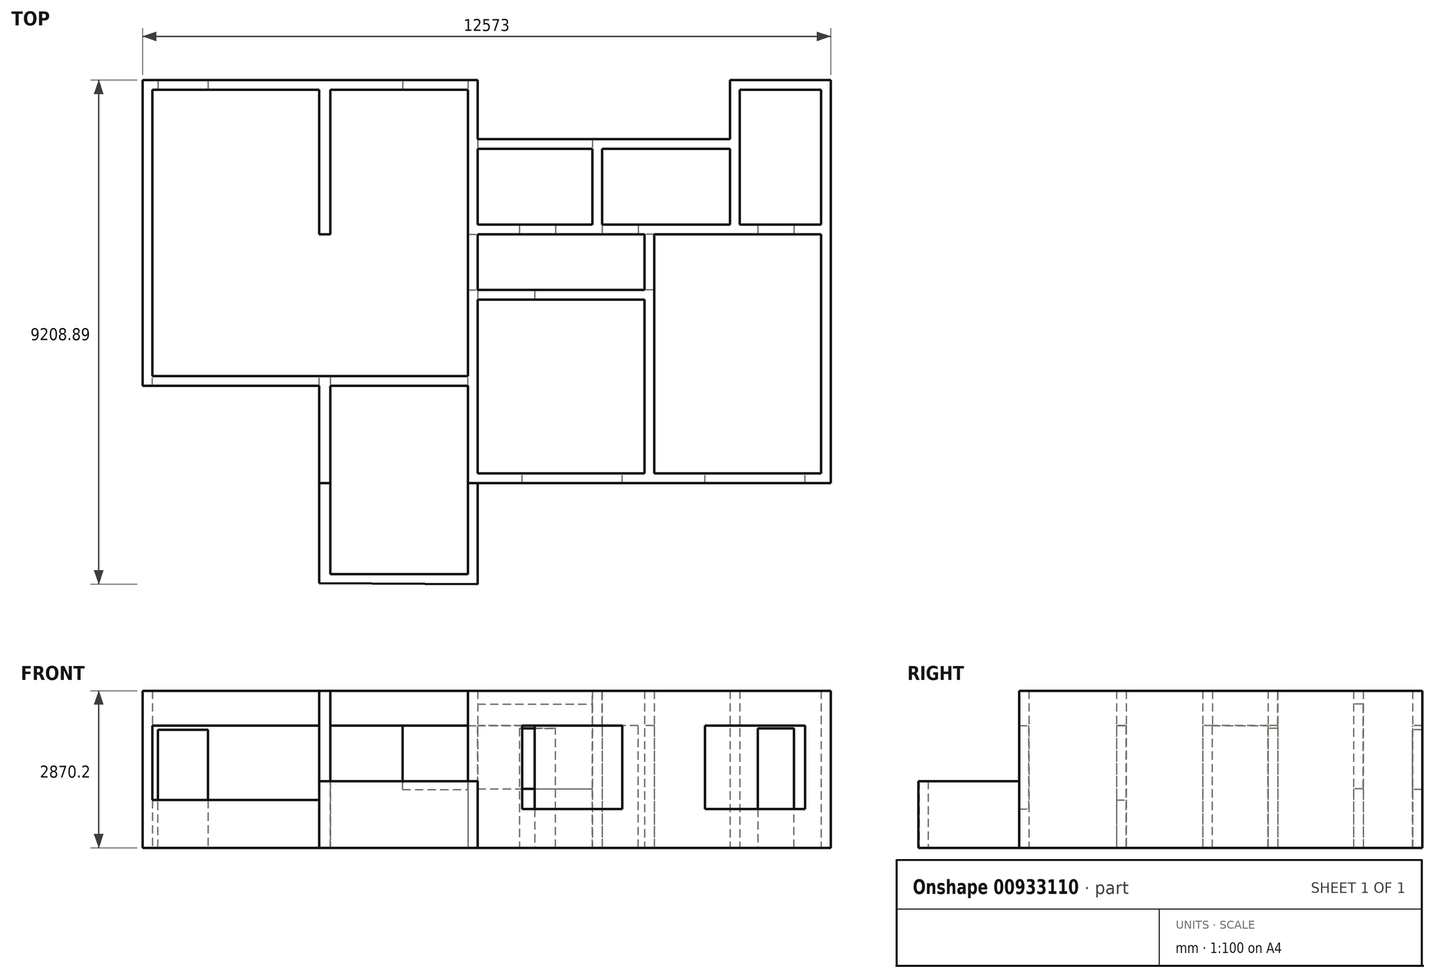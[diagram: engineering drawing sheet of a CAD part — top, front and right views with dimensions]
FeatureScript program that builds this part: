
annotation { "Feature Type Name" : "Feature", "Feature Type Description" : "" }
export const myFeature = defineFeature(function(context is Context, id is Id, definition is map)
    precondition{}
    {
        {
            var Q0;
            Q0=qCreatedBy(makeId("Top.planeOp"),FACE);
            var sketch = newSketch(context, id + "F0", { "sketchPlane" : qUnion([Q0])});
            skLineSegment(sketch, "E0", {"start": v(0, 0) * mm, "end": v(0, 5232.4) * mm});
            skLineSegment(sketch, "E1", {"start": v(0, 5232.4) * mm, "end": v(3048, 5232.4) * mm});
            skLineSegment(sketch, "E2", {"start": v(3048, 5232.4) * mm, "end": v(3048, 2590.8) * mm});
            skLineSegment(sketch, "E3", {"start": v(3251.2, 5232.4) * mm, "end": v(3251.2, 2590.8) * mm});
            skLineSegment(sketch, "E4", {"start": v(3251.2, 2590.8) * mm, "end": v(3048, 2590.8) * mm});
            skLineSegment(sketch, "E5", {"start": v(3251.2, 5232.4) * mm, "end": v(5765.8, 5232.4) * mm});
            skLineSegment(sketch, "E6", {"start": v(5765.8, 0.57) * mm, "end": v(5765.8, 1575.37) * mm});
            skLineSegment(sketch, "E7", {"start": v(5765.8, 5232.4) * mm, "end": v(5765.8, 2590.8) * mm});
            skLineSegment(sketch, "E8", {"start": v(5943.6, 1575.37) * mm, "end": v(8991.6, 1575.37) * mm});
            skLineSegment(sketch, "E9", {"start": v(5943.63, -1777.43) * mm, "end": v(8991.6, -1777.43) * mm});
            skLineSegment(sketch, "E10", {"start": v(9169.4, -1777.43) * mm, "end": v(12217.4, -1777.43) * mm});
            skLineSegment(sketch, "E11", {"start": v(12217.4, -1777.43) * mm, "end": v(12217.4, 2591.37) * mm});
            skLineSegment(sketch, "E12", {"start": v(10553.7, 4153.47) * mm, "end": v(8064.5, 4153.47) * mm});
            skLineSegment(sketch, "E13", {"start": v(10731.5, 5232.97) * mm, "end": v(12217.4, 5232.97) * mm});
            skLineSegment(sketch, "E14", {"start": v(7886.7, 4153.47) * mm, "end": v(5943.6, 4153.47) * mm});
            skLineSegment(sketch, "E15", {"start": v(8991.6, 1575.37) * mm, "end": v(8991.6, 2591.37) * mm});
            skLineSegment(sketch, "E16", {"start": v(5943.6, 2591.37) * mm, "end": v(5943.6, 1575.37) * mm});
            skLineSegment(sketch, "E17", {"start": v(5765.8, 2590.8) * mm, "end": v(5765.8, 1575.37) * mm});
            skLineSegment(sketch, "E18", {"start": v(5943.6, 1397.57) * mm, "end": v(8991.6, 1397.57) * mm});
            skLineSegment(sketch, "E19", {"start": v(8991.6, 1397.57) * mm, "end": v(8991.6, -1777.43) * mm});
            skLineSegment(sketch, "E20", {"start": v(5943.6, 1397.57) * mm, "end": v(5943.63, -1777.43) * mm});
            skLineSegment(sketch, "E21", {"start": v(9169.4, -1777.43) * mm, "end": v(9169.4, 2591.37) * mm});
            skLineSegment(sketch, "E22", {"start": v(5943.6, 4153.47) * mm, "end": v(5943.6, 2769.17) * mm});
            skLineSegment(sketch, "E23", {"start": v(7886.7, 4153.47) * mm, "end": v(7886.7, 2769.17) * mm});
            skLineSegment(sketch, "E24", {"start": v(8064.5, 4153.47) * mm, "end": v(8064.5, 2769.17) * mm});
            skLineSegment(sketch, "E25", {"start": v(5943.6, 2769.17) * mm, "end": v(7886.7, 2769.17) * mm});
            skLineSegment(sketch, "E26", {"start": v(8064.5, 2769.17) * mm, "end": v(10553.7, 2769.17) * mm});
            skLineSegment(sketch, "E27", {"start": v(10553.7, 4153.47) * mm, "end": v(10553.7, 2769.17) * mm});
            skLineSegment(sketch, "E28", {"start": v(5943.6, 2591.37) * mm, "end": v(8991.6, 2591.37) * mm});
            skLineSegment(sketch, "E29", {"start": v(9169.4, 2591.37) * mm, "end": v(12217.4, 2591.37) * mm});
            skLineSegment(sketch, "E30", {"start": v(-177.8, -177.8) * mm, "end": v(-177.8, 5410.2) * mm});
            skLineSegment(sketch, "E31", {"start": v(-177.8, 5410.2) * mm, "end": v(5943.6, 5410.84) * mm});
            skLineSegment(sketch, "E32", {"start": v(10553.7, 4331.34) * mm, "end": v(5943.6, 4331.34) * mm});
            skLineSegment(sketch, "E33", {"start": v(5943.6, 5410.84) * mm, "end": v(5943.6, 4331.34) * mm});
            skLineSegment(sketch, "E34", {"start": v(10553.7, 4331.34) * mm, "end": v(10553.7, 5410.84) * mm});
            skLineSegment(sketch, "E35", {"start": v(10553.7, 5410.84) * mm, "end": v(12395.2, 5410.84) * mm});
            skLineSegment(sketch, "E36", {"start": v(5770.84, -3619.48) * mm, "end": v(3251.23, -3619.5) * mm});
            skLineSegment(sketch, "E37", {"start": v(-177.8, -177.8) * mm, "end": v(3048, -177.8) * mm});
            skLineSegment(sketch, "E38", {"start": v(3048, -177.8) * mm, "end": v(3048.03, -3785.2) * mm});
            skLineSegment(sketch, "E39", {"start": v(12395.2, 5410.84) * mm, "end": v(12395.2, -1955.23) * mm});
            skLineSegment(sketch, "E40", {"start": v(12395.2, -1955.23) * mm, "end": v(5943.6, -1955.23) * mm});
            skLineSegment(sketch, "E41", {"start": v(5943.6, -1955.23) * mm, "end": v(5943.6, -3798.05) * mm});
            skLineSegment(sketch, "E42", {"start": v(3048.03, -3785.2) * mm, "end": v(5943.6, -3798.05) * mm});
            skLineSegment(sketch, "E43", {"start": v(3251.21, -177.8) * mm, "end": v(5765.81, -177.8) * mm});
            skLineSegment(sketch, "E44", {"start": v(3251.21, -177.8) * mm, "end": v(3251.23, -3619.5) * mm});
            skLineSegment(sketch, "E45", {"start": v(0, 0) * mm, "end": v(5765.8, 0.57) * mm});
            skLineSegment(sketch, "E46", {"start": v(5765.81, -177.8) * mm, "end": v(5770.84, -3619.48) * mm});
            skLineSegment(sketch, "E47", {"start": v(10731.5, 5232.97) * mm, "end": v(10731.5, 2769.17) * mm});
            skLineSegment(sketch, "E48", {"start": v(12217.4, 5232.97) * mm, "end": v(12217.4, 2769.17) * mm});
            skLineSegment(sketch, "E49", {"start": v(12217.4, 2769.17) * mm, "end": v(10731.5, 2769.17) * mm});
            skSolve(sketch);
        }
        {
            var Q0;
            Q0=makeQuery(id+"F0.imprint","IMPRINT",FACE,{"disambiguationData":[TD([[makeQuery(id+"F0.imprint","IMPRINT",EDGE,{"derivedFrom":sQuery(id+"F0.wireOp",EDGE,"E0")}),1.0]])]});
            extrude(context, id + "F1", {"entities" : qUnion([Q0]), "depth" : 2870.2 * mm, "offsetDistance" : 25.4 * mm});
        }
        {
            var Q0;
            Q0=makeQuery(id+"F1.opExtrude","SWEPT_FACE",FACE,{"disambiguationData":[OSD([sQuery(id+"F0.wireOp",EDGE,"E1")])]});
            var sketch = newSketch(context, id + "F2", { "sketchPlane" : qUnion([Q0])});
            skLineSegment(sketch, "E50", {"start": v(101.6, 0) * mm, "end": v(101.6, 2159) * mm});
            skLineSegment(sketch, "E51", {"start": v(101.6, 2159) * mm, "end": v(1016, 2159) * mm});
            skLineSegment(sketch, "E52", {"start": v(1016, 2159) * mm, "end": v(1016, 0) * mm});
            skLineSegment(sketch, "E53", {"start": v(1016, 0) * mm, "end": v(101.6, 0) * mm});
            skSolve(sketch);
        }
        {
            var Q0;
            Q0=makeQuery(id+"F2.imprint","IMPRINT",FACE,{"disambiguationData":[TD([[makeQuery(id+"F2.imprint","IMPRINT",EDGE,{"derivedFrom":sQuery(id+"F2.wireOp",EDGE,"E50")}),-1.0]])]});
            extrude(context, id + "F3", {"entities" : qUnion([Q0]), "operationType" : NewBodyOperationType.REMOVE, "endBound" : BoundingType.THROUGH_ALL, "oppositeDirection" : true, "depth" : 25.4 * mm, "offsetDistance" : 25.4 * mm});
        }
        {
            var Q0;
            Q0=makeQuery(id+"F1.opExtrude","SWEPT_FACE",FACE,{"disambiguationData":[OSD([sQuery(id+"F0.wireOp",EDGE,"E45")])]});
            var sketch = newSketch(context, id + "F4", { "sketchPlane" : qUnion([Q0])});
            skLineSegment(sketch, "E54", {"start": v(0, 2870.2) * mm, "end": v(0, 2235.2) * mm});
            skLineSegment(sketch, "E55", {"start": v(0, 2235.2) * mm, "end": v(0, 872.46) * mm});
            skLineSegment(sketch, "E56", {"start": v(0, 2235.2) * mm, "end": v(-2456.97, 2235.2) * mm});
            skLineSegment(sketch, "E57", {"start": v(-2456.97, 2235.2) * mm, "end": v(-2456.97, 872.46) * mm});
            skLineSegment(sketch, "E58", {"start": v(-2456.97, 872.46) * mm, "end": v(0, 872.46) * mm});
            skSolve(sketch);
        }
        {
            var Q0;
            Q0=makeQuery(id+"F4.imprint","IMPRINT",FACE,{"disambiguationData":[TD([[makeQuery(id+"F4.imprint","IMPRINT",EDGE,{"derivedFrom":sQuery(id+"F4.wireOp",EDGE,"E55")}),-1.0]])]});
            extrude(context, id + "F5", {"entities" : qUnion([Q0]), "operationType" : NewBodyOperationType.REMOVE, "endBound" : BoundingType.THROUGH_ALL, "oppositeDirection" : true, "depth" : 25.4 * mm, "offsetDistance" : 25.4 * mm});
        }
        {
            var Q0;
            Q0=makeQuery(id+"F5.boolean.opBoolean","COPY",FACE,{"derivedFrom":makeQuery(id+"F5.opExtrude","SWEPT_FACE",FACE,{"disambiguationData":[OSD([sQuery(id+"F4.wireOp",EDGE,"E57")])]})});
            var Q1;
            Q1=makeQuery(id+"F1.opExtrude","SWEPT_FACE",FACE,{"disambiguationData":[OSD([sQuery(id+"F0.wireOp",EDGE,"E38")])]});
            extrude(context, id + "F6", {"entities" : qUnion([Q0]), "operationType" : NewBodyOperationType.REMOVE, "endBound" : BoundingType.UP_TO_SURFACE, "oppositeDirection" : true, "depth" : 25.4 * mm, "endBoundEntityFace" : qUnion([Q1]), "offsetDistance" : 25.4 * mm});
        }
        {
            var Q0;
            Q0=makeQuery(id+"F1.opExtrude","SWEPT_FACE",FACE,{"disambiguationData":[OSD([sQuery(id+"F0.wireOp",EDGE,"E45")])]});
            var sketch = newSketch(context, id + "F7", { "sketchPlane" : qUnion([Q0])});
            skLineSegment(sketch, "E59", {"start": v(-5765.8, 2235.2) * mm, "end": v(-5765.8, 0) * mm});
            skLineSegment(sketch, "E60", {"start": v(-5765.8, 2235.2) * mm, "end": v(-4114.3, 2235.2) * mm});
            skLineSegment(sketch, "E61", {"start": v(-4114.3, 2235.2) * mm, "end": v(-4114.3, 0) * mm});
            skLineSegment(sketch, "E62", {"start": v(-4114.3, 0) * mm, "end": v(-5765.8, 0) * mm});
            skSolve(sketch);
        }
        {
            var Q0;
            Q0=makeQuery(id+"F7.imprint","IMPRINT",FACE,{"disambiguationData":[TD([[makeQuery(id+"F7.imprint","IMPRINT",EDGE,{"derivedFrom":sQuery(id+"F7.wireOp",EDGE,"E59")}),1.0]])]});
            extrude(context, id + "F8", {"entities" : qUnion([Q0]), "operationType" : NewBodyOperationType.REMOVE, "oppositeDirection" : true, "depth" : 203.2 * mm, "offsetDistance" : 25.4 * mm});
        }
        {
            var Q0;
            Q0=makeQuery(id+"F8.boolean.opBoolean","COPY",FACE,{"derivedFrom":makeQuery(id+"F8.opExtrude","SWEPT_FACE",FACE,{"disambiguationData":[OSD([sQuery(id+"F7.wireOp",EDGE,"E61")])]})});
            var Q1;
            Q1=makeQuery(id+"F1.opExtrude","SWEPT_FACE",FACE,{"disambiguationData":[OSD([sQuery(id+"F0.wireOp",EDGE,"E44")])]});
            extrude(context, id + "F9", {"entities" : qUnion([Q0]), "operationType" : NewBodyOperationType.REMOVE, "endBound" : BoundingType.UP_TO_SURFACE, "oppositeDirection" : true, "depth" : 25.4 * mm, "endBoundEntityFace" : qUnion([Q1]), "offsetDistance" : 25.4 * mm});
        }
        {
            var Q0;
            Q0=makeQuery(id+"F1.opExtrude","SWEPT_FACE",FACE,{"disambiguationData":[OSD([sQuery(id+"F0.wireOp",EDGE,"E42")])]});
            var sketch = newSketch(context, id + "F10", { "sketchPlane" : qUnion([Q0])});
            skLineSegment(sketch, "E63", {"start": v(5960.4, 2870.2) * mm, "end": v(5960.4, 1219.2) * mm});
            skLineSegment(sketch, "E64", {"start": v(2907.05, 2870.2) * mm, "end": v(5960.4, 2870.2) * mm});
            skLineSegment(sketch, "E65", {"start": v(5960.4, 1219.2) * mm, "end": v(5397.9, 1219.2) * mm});
            skLineSegment(sketch, "E66", {"start": v(5397.9, 1219.2) * mm, "end": v(5397.9, 2870.2) * mm});
            skLineSegment(sketch, "E67", {"start": v(5397.9, 2870.2) * mm, "end": v(5960.4, 2870.2) * mm});
            skSolve(sketch);
        }
        {
            var Q0;
            Q0=makeQuery(id+"F1.opExtrude","SWEPT_FACE",FACE,{"disambiguationData":[OSD([sQuery(id+"F0.wireOp",EDGE,"E16")])]});
            var sketch = newSketch(context, id + "F11", { "sketchPlane" : qUnion([Q0])});
            skLineSegment(sketch, "E68", {"start": v(1575.37, 2235.2) * mm, "end": v(1575.37, 0) * mm});
            skLineSegment(sketch, "E69", {"start": v(1575.37, 0) * mm, "end": v(2591.37, 0) * mm});
            skLineSegment(sketch, "E70", {"start": v(2591.37, 0) * mm, "end": v(2591.37, 2235.2) * mm});
            skLineSegment(sketch, "E71", {"start": v(2591.37, 2235.2) * mm, "end": v(1575.37, 2235.2) * mm});
            skSolve(sketch);
        }
        {
            var Q0;
            Q0=makeQuery(id+"F11.imprint","IMPRINT",FACE,{"disambiguationData":[TD([[makeQuery(id+"F11.imprint","IMPRINT",EDGE,{"derivedFrom":sQuery(id+"F11.wireOp",EDGE,"E68")}),1.0]])]});
            extrude(context, id + "F12", {"entities" : qUnion([Q0]), "operationType" : NewBodyOperationType.REMOVE, "oppositeDirection" : true, "depth" : 406.4 * mm, "offsetDistance" : 25.4 * mm});
        }
        {
            var Q0;
            Q0=makeQuery(id+"F1.opExtrude","SWEPT_FACE",FACE,{"disambiguationData":[OSD([sQuery(id+"F0.wireOp",EDGE,"E15")])]});
            var sketch = newSketch(context, id + "F13", { "sketchPlane" : qUnion([Q0])});
            skLineSegment(sketch, "E72", {"start": v(-2591.37, 2870.2) * mm, "end": v(-2591.37, 2235.2) * mm});
            skLineSegment(sketch, "E73", {"start": v(-2591.37, 2235.2) * mm, "end": v(-2591.37, 0) * mm});
            skLineSegment(sketch, "E74", {"start": v(-2591.37, 0) * mm, "end": v(-1575.37, 0) * mm});
            skLineSegment(sketch, "E75", {"start": v(-1575.37, 0) * mm, "end": v(-1575.37, 2235.2) * mm});
            skLineSegment(sketch, "E76", {"start": v(-1575.37, 2235.2) * mm, "end": v(-2591.37, 2235.2) * mm});
            skSolve(sketch);
        }
        {
            var Q0;
            Q0=makeQuery(id+"F13.imprint","IMPRINT",FACE,{"disambiguationData":[TD([[makeQuery(id+"F13.imprint","IMPRINT",EDGE,{"derivedFrom":sQuery(id+"F13.wireOp",EDGE,"E73")}),1.0]])]});
            extrude(context, id + "F14", {"entities" : qUnion([Q0]), "operationType" : NewBodyOperationType.REMOVE, "oppositeDirection" : true, "depth" : 457.2 * mm, "offsetDistance" : 25.4 * mm});
        }
        {
            var Q0;
            Q0=makeQuery(id+"F1.opExtrude","SWEPT_FACE",FACE,{"disambiguationData":[OSD([sQuery(id+"F0.wireOp",EDGE,"E5")])]});
            var sketch = newSketch(context, id + "F15", { "sketchPlane" : qUnion([Q0])});
            skLineSegment(sketch, "E77", {"start": v(5765.8, 2235.2) * mm, "end": v(5765.8, 1066.8) * mm});
            skLineSegment(sketch, "E78", {"start": v(5765.8, 1066.8) * mm, "end": v(4572, 1066.8) * mm});
            skLineSegment(sketch, "E79", {"start": v(4572, 1066.8) * mm, "end": v(4572, 2235.2) * mm});
            skLineSegment(sketch, "E80", {"start": v(4572, 2235.2) * mm, "end": v(5765.8, 2235.2) * mm});
            skSolve(sketch);
        }
        {
            var Q0;
            Q0=makeQuery(id+"F15.imprint","IMPRINT",FACE,{"disambiguationData":[TD([[makeQuery(id+"F15.imprint","IMPRINT",EDGE,{"derivedFrom":sQuery(id+"F15.wireOp",EDGE,"E77")}),-1.0]])]});
            extrude(context, id + "F16", {"entities" : qUnion([Q0]), "operationType" : NewBodyOperationType.REMOVE, "oppositeDirection" : true, "depth" : 381 * mm, "offsetDistance" : 25.4 * mm});
        }
        {
            var Q0;
            Q0=makeQuery(id+"F14.boolean.opBoolean","MERGE",FACE,{"derivedFrom":[makeQuery(id+"F1.opExtrude","SWEPT_FACE",FACE,{"disambiguationData":[OSD([sQuery(id+"F0.wireOp",EDGE,"E29")])]}),makeQuery(id+"F12.boolean.opBoolean","MERGE",FACE,{"derivedFrom":[makeQuery(id+"F1.opExtrude","SWEPT_FACE",FACE,{"disambiguationData":[OSD([sQuery(id+"F0.wireOp",EDGE,"E28")])]})],"fromTools":[makeQuery(id+"F12.opExtrude","SWEPT_FACE",FACE,{"disambiguationData":[OSD([sQuery(id+"F11.wireOp",EDGE,"E70")])]})]})],"fromTools":[makeQuery(id+"F14.opExtrude","SWEPT_FACE",FACE,{"disambiguationData":[OSD([sQuery(id+"F13.wireOp",EDGE,"E73")])]})]});
            var sketch = newSketch(context, id + "F17", { "sketchPlane" : qUnion([Q0])});
            skLineSegment(sketch, "E81", {"start": v(6707.64, 0) * mm, "end": v(7368.04, 0) * mm});
            skLineSegment(sketch, "E82", {"start": v(7368.04, 0) * mm, "end": v(7368.04, 2184.4) * mm});
            skLineSegment(sketch, "E83", {"start": v(7368.04, 2184.4) * mm, "end": v(6707.64, 2184.4) * mm});
            skLineSegment(sketch, "E84", {"start": v(6707.64, 2184.4) * mm, "end": v(6707.64, 0) * mm});
            skSolve(sketch);
        }
        {
            var Q0;
            Q0=makeQuery(id+"F17.imprint","IMPRINT",FACE,{"disambiguationData":[TD([[makeQuery(id+"F17.imprint","IMPRINT",EDGE,{"derivedFrom":sQuery(id+"F17.wireOp",EDGE,"E81")}),1.0]])]});
            extrude(context, id + "F18", {"entities" : qUnion([Q0]), "operationType" : NewBodyOperationType.REMOVE, "oppositeDirection" : true, "depth" : 330.2 * mm, "offsetDistance" : 25.4 * mm});
        }
        {
            var Q0;
            Q0=makeQuery(id+"F14.boolean.opBoolean","MERGE",FACE,{"derivedFrom":[makeQuery(id+"F1.opExtrude","SWEPT_FACE",FACE,{"disambiguationData":[OSD([sQuery(id+"F0.wireOp",EDGE,"E29")])]}),makeQuery(id+"F12.boolean.opBoolean","MERGE",FACE,{"derivedFrom":[makeQuery(id+"F1.opExtrude","SWEPT_FACE",FACE,{"disambiguationData":[OSD([sQuery(id+"F0.wireOp",EDGE,"E28")])]})],"fromTools":[makeQuery(id+"F12.opExtrude","SWEPT_FACE",FACE,{"disambiguationData":[OSD([sQuery(id+"F11.wireOp",EDGE,"E70")])]})]})],"fromTools":[makeQuery(id+"F14.opExtrude","SWEPT_FACE",FACE,{"disambiguationData":[OSD([sQuery(id+"F13.wireOp",EDGE,"E73")])]})]});
            var sketch = newSketch(context, id + "F19", { "sketchPlane" : qUnion([Q0])});
            skLineSegment(sketch, "E85", {"start": v(8218.94, 0) * mm, "end": v(8879.34, 0) * mm});
            skLineSegment(sketch, "E86", {"start": v(8879.34, 0) * mm, "end": v(8879.34, 2235.2) * mm});
            skLineSegment(sketch, "E87", {"start": v(8879.34, 2235.2) * mm, "end": v(8218.94, 2235.2) * mm});
            skLineSegment(sketch, "E88", {"start": v(8218.94, 2235.2) * mm, "end": v(8218.94, 0) * mm});
            skSolve(sketch);
        }
        {
            var Q0;
            Q0=makeQuery(id+"F19.imprint","IMPRINT",FACE,{"disambiguationData":[TD([[makeQuery(id+"F19.imprint","IMPRINT",EDGE,{"derivedFrom":sQuery(id+"F19.wireOp",EDGE,"E85")}),1.0]])]});
            var Q1;
            Q1=makeQuery(id+"F1.opExtrude","SWEPT_FACE",FACE,{"disambiguationData":[OSD([sQuery(id+"F0.wireOp",EDGE,"E12")])]});
            extrude(context, id + "F20", {"entities" : qUnion([Q0]), "operationType" : NewBodyOperationType.REMOVE, "endBound" : BoundingType.UP_TO_SURFACE, "oppositeDirection" : true, "depth" : 304.8 * mm, "endBoundEntityFace" : qUnion([Q1]), "offsetDistance" : 25.4 * mm});
        }
        {
            var Q0;
            Q0=makeQuery(id+"F1.opExtrude","SWEPT_FACE",FACE,{"disambiguationData":[OSD([sQuery(id+"F0.wireOp",EDGE,"E24")])]});
            extrude(context, id + "F21", {"entities" : qUnion([Q0]), "operationType" : NewBodyOperationType.REMOVE, "oppositeDirection" : true, "depth" : 685.8 * mm, "offsetDistance" : 25.4 * mm});
        }
        {
            var Q0;
            {var subQ0=sQuery(id+"F0.wireOp",EDGE,"E26");Q0=makeQuery(id+"F21.boolean.opBoolean","MERGE",FACE,{"derivedFrom":[makeQuery(id+"F1.opExtrude","SWEPT_FACE",FACE,{"disambiguationData":[OSD([subQ0])]}),makeQuery(id+"F1.opExtrude","SWEPT_FACE",FACE,{"disambiguationData":[OSD([sQuery(id+"F0.wireOp",EDGE,"E25")])]})],"fromTools":[makeQuery(id+"F21.opExtrude","SWEPT_FACE",FACE,{"disambiguationData":[OSD([sQuery(id+"F0.wireOp",EDGE,"E24"),subQ0])]})]});}
            var sketch = newSketch(context, id + "F22", { "sketchPlane" : qUnion([Q0])});
            skLineSegment(sketch, "E89", {"start": v(-8218.94, 0) * mm, "end": v(-8218.94, 2870.2) * mm});
            skLineSegment(sketch, "E90", {"start": v(-8218.94, 2870.2) * mm, "end": v(-8041.14, 2870.2) * mm});
            skLineSegment(sketch, "E91", {"start": v(-8041.14, 2870.2) * mm, "end": v(-8041.14, 0) * mm});
            skLineSegment(sketch, "E92", {"start": v(-8041.14, 0) * mm, "end": v(-8218.94, 0) * mm});
            skSolve(sketch);
        }
        {
            var Q0;
            {var subQ0=sQuery(id+"F22.wireOp",EDGE,"E90");Q0=makeQuery(id+"F22.imprint","IMPRINT",FACE,{"disambiguationData":[TD([[makeQuery(id+"F22.imprint","IMPRINT",EDGE,{"derivedFrom":subQ0}),1.0]])]});}
            var Q1;
            {var subQ0=sQuery(id+"F0.wireOp",EDGE,"E12");Q1=makeQuery(id+"F21.boolean.opBoolean","MERGE",FACE,{"derivedFrom":[makeQuery(id+"F20.boolean.opBoolean","MERGE",FACE,{"derivedFrom":[makeQuery(id+"F1.opExtrude","SWEPT_FACE",FACE,{"disambiguationData":[OSD([subQ0])]}),makeQuery(id+"F1.opExtrude","SWEPT_FACE",FACE,{"disambiguationData":[OSD([sQuery(id+"F0.wireOp",EDGE,"E14")])]})],"fromTools":[makeQuery(id+"F20.opExtrude","CAP_FACE",FACE,{"disambiguationData":[OSD([sQuery(id+"F19.wireOp",EDGE,"E85"),sQuery(id+"F19.wireOp",EDGE,"E86"),sQuery(id+"F19.wireOp",EDGE,"E87"),sQuery(id+"F19.wireOp",EDGE,"E88")])],"isStart":false})]})],"fromTools":[makeQuery(id+"F21.opExtrude","SWEPT_FACE",FACE,{"disambiguationData":[OSD([subQ0,sQuery(id+"F0.wireOp",EDGE,"E24")])]})]});}
            extrude(context, id + "F23", {"entities" : qUnion([Q0]), "operationType" : NewBodyOperationType.ADD, "endBound" : BoundingType.UP_TO_SURFACE, "depth" : 25.4 * mm, "endBoundEntityFace" : qUnion([Q1]), "offsetDistance" : 25.4 * mm});
        }
        {
            var Q0;
            Q0=makeQuery(id+"F14.boolean.opBoolean","MERGE",FACE,{"derivedFrom":[makeQuery(id+"F1.opExtrude","SWEPT_FACE",FACE,{"disambiguationData":[OSD([sQuery(id+"F0.wireOp",EDGE,"E29")])]}),makeQuery(id+"F12.boolean.opBoolean","MERGE",FACE,{"derivedFrom":[makeQuery(id+"F1.opExtrude","SWEPT_FACE",FACE,{"disambiguationData":[OSD([sQuery(id+"F0.wireOp",EDGE,"E28")])]})],"fromTools":[makeQuery(id+"F12.opExtrude","SWEPT_FACE",FACE,{"disambiguationData":[OSD([sQuery(id+"F11.wireOp",EDGE,"E70")])]})]})],"fromTools":[makeQuery(id+"F14.opExtrude","SWEPT_FACE",FACE,{"disambiguationData":[OSD([sQuery(id+"F13.wireOp",EDGE,"E73")])]})]});
            var sketch = newSketch(context, id + "F24", { "sketchPlane" : qUnion([Q0])});
            skLineSegment(sketch, "E93", {"start": v(11723.04, 0) * mm, "end": v(11723.04, 2184.4) * mm});
            skLineSegment(sketch, "E94", {"start": v(11723.04, 2184.4) * mm, "end": v(11062.64, 2184.4) * mm});
            skLineSegment(sketch, "E95", {"start": v(11062.64, 2184.4) * mm, "end": v(11062.64, 0) * mm});
            skLineSegment(sketch, "E96", {"start": v(11062.64, 0) * mm, "end": v(11723.04, 0) * mm});
            skSolve(sketch);
        }
        {
            var Q0;
            Q0=makeQuery(id+"F24.imprint","IMPRINT",FACE,{"disambiguationData":[TD([[makeQuery(id+"F24.imprint","IMPRINT",EDGE,{"derivedFrom":sQuery(id+"F24.wireOp",EDGE,"E93")}),1.0]])]});
            extrude(context, id + "F25", {"entities" : qUnion([Q0]), "operationType" : NewBodyOperationType.REMOVE, "oppositeDirection" : true, "depth" : 381 * mm, "offsetDistance" : 25.4 * mm});
        }
        {
            var Q0;
            Q0=makeQuery(id+"F1.opExtrude","SWEPT_FACE",FACE,{"disambiguationData":[OSD([sQuery(id+"F0.wireOp",EDGE,"E18")])]});
            var sketch = newSketch(context, id + "F26", { "sketchPlane" : qUnion([Q0])});
            skLineSegment(sketch, "E97", {"start": v(5943.6, 2235.2) * mm, "end": v(6984.7, 2235.2) * mm});
            skLineSegment(sketch, "E98", {"start": v(6984.7, 2235.2) * mm, "end": v(6984.7, 0) * mm});
            skLineSegment(sketch, "E99", {"start": v(6984.7, 0) * mm, "end": v(5943.6, 0) * mm});
            skLineSegment(sketch, "E100", {"start": v(5943.6, 0) * mm, "end": v(5943.6, 2235.2) * mm});
            skSolve(sketch);
        }
        {
            var Q0;
            Q0=makeQuery(id+"F26.imprint","IMPRINT",FACE,{"disambiguationData":[TD([[makeQuery(id+"F26.imprint","IMPRINT",EDGE,{"derivedFrom":sQuery(id+"F26.wireOp",EDGE,"E97")}),-1.0]])]});
            extrude(context, id + "F27", {"entities" : qUnion([Q0]), "operationType" : NewBodyOperationType.REMOVE, "oppositeDirection" : true, "depth" : 279.4 * mm, "offsetDistance" : 25.4 * mm});
        }
        {
            var Q0;
            Q0=makeQuery(id+"F1.opExtrude","SWEPT_FACE",FACE,{"disambiguationData":[OSD([sQuery(id+"F0.wireOp",EDGE,"E9")])]});
            var sketch = newSketch(context, id + "F28", { "sketchPlane" : qUnion([Q0])});
            skLineSegment(sketch, "E101", {"start": v(-8586.37, 2235.2) * mm, "end": v(-6757.57, 2235.2) * mm});
            skLineSegment(sketch, "E102", {"start": v(-6757.57, 2235.2) * mm, "end": v(-6757.57, 711.2) * mm});
            skLineSegment(sketch, "E103", {"start": v(-6757.57, 711.2) * mm, "end": v(-8586.37, 711.2) * mm});
            skLineSegment(sketch, "E104", {"start": v(-8586.37, 711.2) * mm, "end": v(-8586.37, 2235.2) * mm});
            skSolve(sketch);
        }
        {
            var Q0;
            Q0=makeQuery(id+"F28.imprint","IMPRINT",FACE,{"disambiguationData":[TD([[makeQuery(id+"F28.imprint","IMPRINT",EDGE,{"derivedFrom":sQuery(id+"F28.wireOp",EDGE,"E101")}),-1.0]])]});
            extrude(context, id + "F29", {"entities" : qUnion([Q0]), "operationType" : NewBodyOperationType.REMOVE, "oppositeDirection" : true, "depth" : 990.6 * mm, "offsetDistance" : 25.4 * mm});
        }
        {
            var Q0;
            Q0=makeQuery(id+"F1.opExtrude","SWEPT_FACE",FACE,{"disambiguationData":[OSD([sQuery(id+"F0.wireOp",EDGE,"E10")])]});
            var sketch = newSketch(context, id + "F30", { "sketchPlane" : qUnion([Q0])});
            skLineSegment(sketch, "E105", {"start": v(-11926.24, 2235.2) * mm, "end": v(-10097.44, 2235.2) * mm});
            skLineSegment(sketch, "E106", {"start": v(-10097.44, 2235.2) * mm, "end": v(-10097.44, 711.2) * mm});
            skLineSegment(sketch, "E107", {"start": v(-10097.44, 711.2) * mm, "end": v(-11926.24, 711.2) * mm});
            skLineSegment(sketch, "E108", {"start": v(-11926.24, 711.2) * mm, "end": v(-11926.24, 2235.2) * mm});
            skSolve(sketch);
        }
        {
            var Q0;
            Q0=makeQuery(id+"F30.imprint","IMPRINT",FACE,{"disambiguationData":[TD([[makeQuery(id+"F30.imprint","IMPRINT",EDGE,{"derivedFrom":sQuery(id+"F30.wireOp",EDGE,"E105")}),-1.0]])]});
            extrude(context, id + "F31", {"entities" : qUnion([Q0]), "operationType" : NewBodyOperationType.REMOVE, "oppositeDirection" : true, "depth" : 304.8 * mm, "offsetDistance" : 25.4 * mm});
        }
        {
            var Q0;
            {var subQ0=sQuery(id+"F0.wireOp",EDGE,"E22");var subQ26=sQuery(id+"F0.wireOp",EDGE,"E24");var subQ35=sQuery(id+"F0.wireOp",EDGE,"E14");var subQ37=sQuery(id+"F0.wireOp",EDGE,"E12");Q0=makeQuery(id+"F23.boolean.opBoolean","SPLIT",FACE,{"disambiguationData":[TD([makeQuery(id+"F1.opExtrude","SWEPT_FACE",FACE,{"disambiguationData":[OSD([subQ0])]})])],"derivedFrom":makeQuery(id+"F21.boolean.opBoolean","MERGE",FACE,{"derivedFrom":[makeQuery(id+"F20.boolean.opBoolean","MERGE",FACE,{"derivedFrom":[makeQuery(id+"F1.opExtrude","SWEPT_FACE",FACE,{"disambiguationData":[OSD([subQ37])]}),makeQuery(id+"F1.opExtrude","SWEPT_FACE",FACE,{"disambiguationData":[OSD([subQ35])]})],"fromTools":[makeQuery(id+"F20.opExtrude","CAP_FACE",FACE,{"disambiguationData":[OSD([sQuery(id+"F19.wireOp",EDGE,"E85"),sQuery(id+"F19.wireOp",EDGE,"E86"),sQuery(id+"F19.wireOp",EDGE,"E87"),sQuery(id+"F19.wireOp",EDGE,"E88")])],"isStart":false})]})],"fromTools":[makeQuery(id+"F21.opExtrude","SWEPT_FACE",FACE,{"disambiguationData":[OSD([subQ37,subQ26])]})]})});}
            var sketch = newSketch(context, id + "F32", { "sketchPlane" : qUnion([Q0])});
            skLineSegment(sketch, "E109", {"start": v(5943.6, 2628.9) * mm, "end": v(8041.14, 2628.9) * mm});
            skLineSegment(sketch, "E110", {"start": v(5943.6, 1079.5) * mm, "end": v(8041.14, 1079.5) * mm});
            skLineSegment(sketch, "E111", {"start": v(5943.6, 2628.9) * mm, "end": v(5943.6, 1079.5) * mm});
            skLineSegment(sketch, "E112", {"start": v(8041.14, 2628.9) * mm, "end": v(8041.14, 1079.5) * mm});
            skSolve(sketch);
        }
        {
            var Q0;
            Q0=makeQuery(id+"F32.imprint","IMPRINT",FACE,{"disambiguationData":[TD([[makeQuery(id+"F32.imprint","IMPRINT",EDGE,{"derivedFrom":sQuery(id+"F32.wireOp",EDGE,"E109")}),-1.0]])]});
            extrude(context, id + "F33", {"entities" : qUnion([Q0]), "operationType" : NewBodyOperationType.REMOVE, "oppositeDirection" : true, "depth" : 304.8 * mm, "offsetDistance" : 25.4 * mm});
        }
        {
            var Q0;
            Q0=makeQuery(id+"F10.imprint","IMPRINT",FACE,{"disambiguationData":[TD([[makeQuery(id+"F10.imprint","IMPRINT",EDGE,{"derivedFrom":sQuery(id+"F10.wireOp",EDGE,"E63")}),-1.0]])]});
            var Q1;
            Q1=makeQuery(id+"F1.opExtrude","SWEPT_FACE",FACE,{"disambiguationData":[OSD([sQuery(id+"F0.wireOp",EDGE,"E40")])]});
            extrude(context, id + "F34", {"entities" : qUnion([Q0]), "operationType" : NewBodyOperationType.REMOVE, "endBound" : BoundingType.UP_TO_SURFACE, "oppositeDirection" : true, "depth" : 25.4 * mm, "endBoundEntityFace" : qUnion([Q1]), "offsetDistance" : 25.4 * mm});
        }
        {
            var Q0;
            Q0=makeQuery(id+"F34.boolean.opBoolean","COPY",FACE,{"derivedFrom":makeQuery(id+"F34.opExtrude","SWEPT_FACE",FACE,{"disambiguationData":[OSD([sQuery(id+"F10.wireOp",EDGE,"E66")])]})});
            var Q1;
            Q1=makeQuery(id+"F1.opExtrude","SWEPT_FACE",FACE,{"disambiguationData":[OSD([sQuery(id+"F0.wireOp",EDGE,"E38")])]});
            extrude(context, id + "F35", {"entities" : qUnion([Q0]), "operationType" : NewBodyOperationType.REMOVE, "endBound" : BoundingType.UP_TO_SURFACE, "oppositeDirection" : true, "depth" : 25.4 * mm, "endBoundEntityFace" : qUnion([Q1]), "offsetDistance" : 25.4 * mm});
        }
        {
            var Q0;
            Q0=makeQuery(id+"F1.opExtrude","SWEPT_FACE",FACE,{"disambiguationData":[OSD([sQuery(id+"F0.wireOp",EDGE,"E38")])]});
            extrude(context, id + "F36", {"entities" : qUnion([Q0]), "operationType" : NewBodyOperationType.ADD, "oppositeDirection" : true, "depth" : 203.2 * mm, "offsetDistance" : 25.4 * mm});
        }
        {
            var Q0;
            Q0=makeQuery(id+"F35.boolean.opBoolean","COPY",FACE,{"derivedFrom":makeQuery(id+"F35.opExtrude","SWEPT_FACE",FACE,{"disambiguationData":[OSD([sQuery(id+"F0.wireOp",EDGE,"E36"),sQuery(id+"F10.wireOp",EDGE,"E66")])]})});
            var Q1;
            Q1=makeQuery(id+"F34.boolean.opBoolean","MERGE",FACE,{"derivedFrom":[makeQuery(id+"F1.opExtrude","SWEPT_FACE",FACE,{"disambiguationData":[OSD([sQuery(id+"F0.wireOp",EDGE,"E40")])]})],"fromTools":[makeQuery(id+"F34.opExtrude","CAP_FACE",FACE,{"disambiguationData":[OSD([sQuery(id+"F10.wireOp",EDGE,"E63"),sQuery(id+"F10.wireOp",EDGE,"E65"),sQuery(id+"F10.wireOp",EDGE,"E66"),sQuery(id+"F10.wireOp",EDGE,"E67")])],"isStart":false})]});
            extrude(context, id + "F37", {"entities" : qUnion([Q0]), "operationType" : NewBodyOperationType.REMOVE, "endBound" : BoundingType.UP_TO_SURFACE, "oppositeDirection" : true, "depth" : 25.4 * mm, "endBoundEntityFace" : qUnion([Q1]), "offsetDistance" : 25.4 * mm});
        }
        {
            var Q0;
            {var subQ0=sQuery(id+"F10.wireOp",EDGE,"E66");var subQ1=sQuery(id+"F0.wireOp",EDGE,"E36");Q0=makeQuery(id+"F37.boolean.opBoolean","COPY",FACE,{"derivedFrom":makeQuery(id+"F37.opExtrude","SWEPT_FACE",FACE,{"disambiguationData":[OSD([subQ1,subQ0]),TDD([makeQuery(id+"F35.boolean.opBoolean","COPY",EDGE,{"derivedFrom":makeQuery(id+"F35.opExtrude","CAP_EDGE",EDGE,{"disambiguationData":[OSD([subQ1,subQ0])],"isStart":false})})])]})});}
            extrude(context, id + "F38", {"entities" : qUnion([Q0]), "operationType" : NewBodyOperationType.REMOVE, "oppositeDirection" : true, "depth" : 25.4 * mm, "offsetDistance" : 25.4 * mm});
        }
        {
            var Q0;
            Q0=makeQuery(id+"F6.boolean.opBoolean","COPY",FACE,{"derivedFrom":makeQuery(id+"F6.opExtrude","SWEPT_FACE",FACE,{"disambiguationData":[OSD([sQuery(id+"F0.wireOp",EDGE,"E37"),sQuery(id+"F4.wireOp",EDGE,"E57")])]})});
            extrude(context, id + "F39", {"entities" : qUnion([Q0]), "operationType" : NewBodyOperationType.REMOVE, "oppositeDirection" : true, "depth" : 25.4 * mm, "offsetDistance" : 25.4 * mm});
        }
    });
